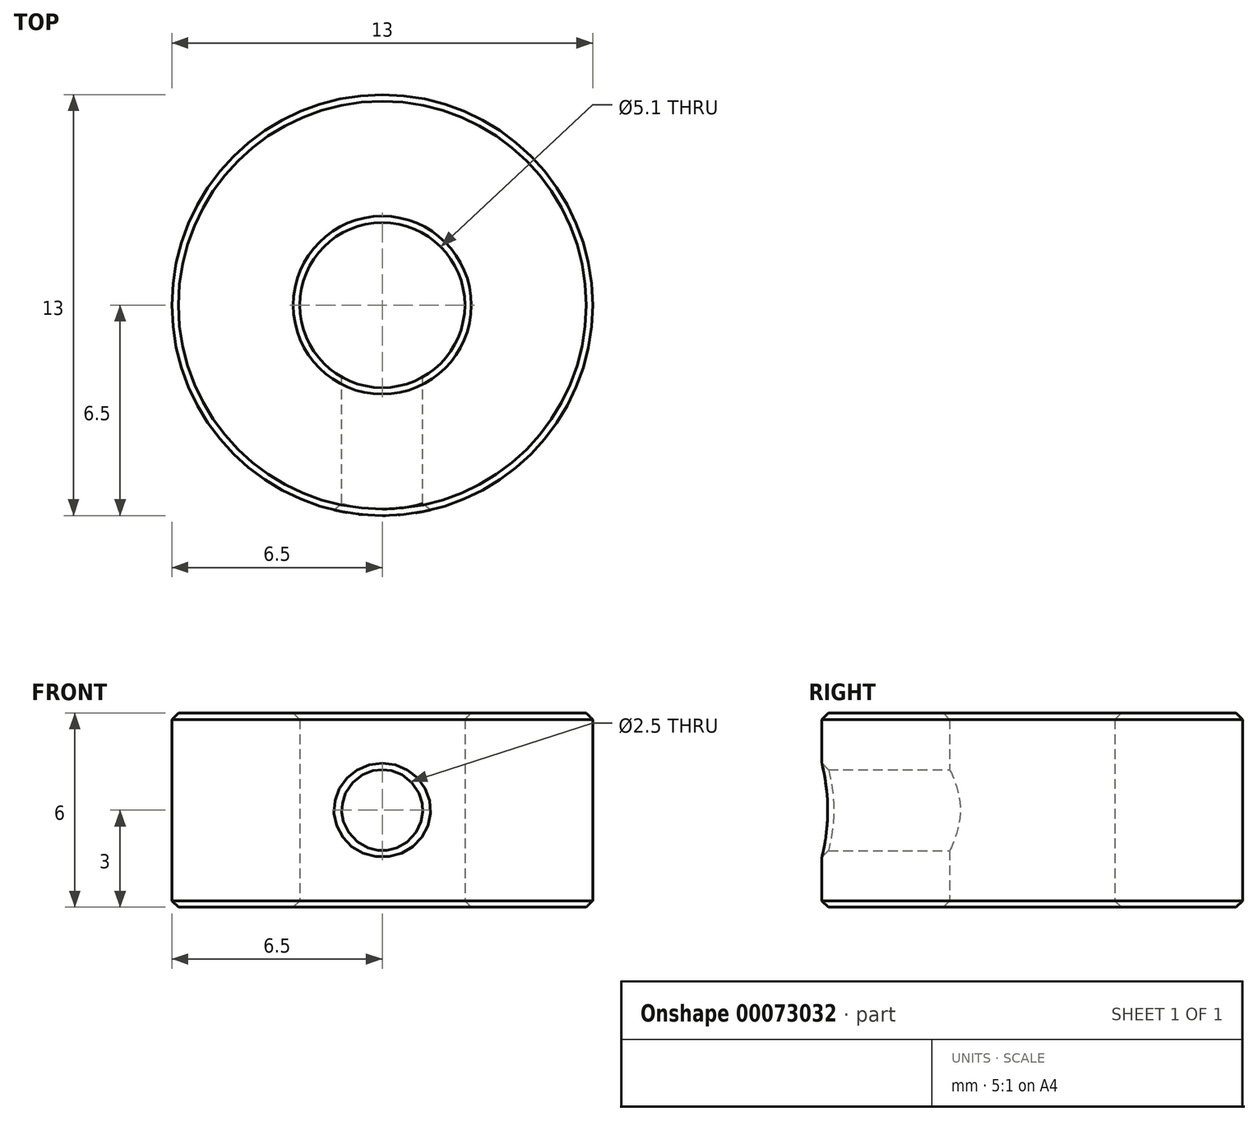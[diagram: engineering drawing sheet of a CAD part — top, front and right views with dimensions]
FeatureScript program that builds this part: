
annotation { "Feature Type Name" : "Feature", "Feature Type Description" : "" }
export const myFeature = defineFeature(function(context is Context, id is Id, definition is map)
    precondition{}
    {
        {
            var Q0;
            Q0=qCreatedBy(makeId("Top.planeOp"),FACE);
            var sketch = newSketch(context, id + "F0", { "sketchPlane" : qUnion([Q0])});
            skCircle(sketch, "E0", {"center": v(0, 0) * mm, "radius": 6.5 * mm});
            skCircle(sketch, "E1", {"center": v(0, 0) * mm, "radius": 2.55 * mm});
            skSolve(sketch);
        }
        {
            var Q0;
            Q0 = qSketchRegion(id + "F0", true);
            extrude(context, id + "F1", {"entities" : qUnion([Q0]), "depth" : 6 * mm});
        }
        {
            var Q0;
            Q0=qCreatedBy(makeId("Front.planeOp"),FACE);
            var sketch = newSketch(context, id + "F2", { "sketchPlane" : qUnion([Q0])});
            skCircle(sketch, "E2", {"center": v(0, 3) * mm, "radius": 1.25 * mm});
            skSolve(sketch);
        }
        {
            var Q0;
            Q0 = qSketchRegion(id + "F2", true);
            extrude(context, id + "F3", {"entities" : qUnion([Q0]), "operationType" : NewBodyOperationType.REMOVE, "endBound" : BoundingType.THROUGH_ALL, "depth" : 25 * mm});
        }
        {
            var Q0;
            Q0=makeQuery(id+"F1.opExtrude","CAP_EDGE",EDGE,{"disambiguationData":[OSD([sQuery(id+"F0.wireOp",EDGE,"E0")])],"isStart":false});
            var Q1;
            Q1=makeQuery(id+"F1.opExtrude","CAP_EDGE",EDGE,{"disambiguationData":[OSD([sQuery(id+"F0.wireOp",EDGE,"E0")])],"isStart":true});
            var Q2;
            Q2=makeQuery(id+"F1.opExtrude","CAP_EDGE",EDGE,{"disambiguationData":[OSD([sQuery(id+"F0.wireOp",EDGE,"E1")])],"isStart":false});
            var Q3;
            Q3=makeQuery(id+"F1.opExtrude","CAP_EDGE",EDGE,{"disambiguationData":[OSD([sQuery(id+"F0.wireOp",EDGE,"E1")])],"isStart":true});
            var Q4;
            Q4=makeQuery(id+"F3.boolean.opBoolean","INTERSECT",EDGE,{"derivedFrom":[makeQuery(id+"F1.opExtrude","SWEPT_FACE",FACE,{"disambiguationData":[OSD([sQuery(id+"F0.wireOp",EDGE,"E0")])]}),makeQuery(id+"F3.opExtrude","SWEPT_FACE",FACE,{"disambiguationData":[OSD([sQuery(id+"F2.wireOp",EDGE,"E2")])]})]});
            chamfer(context, id + "F4", {"entities" : qUnion([Q0, Q1, Q2, Q3, Q4]), "width" : 0.2 * mm, "tangentPropagation" : true});
        }
    });
